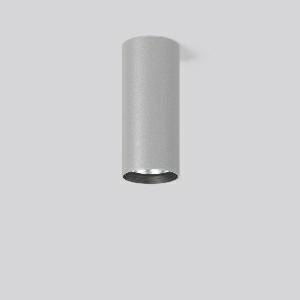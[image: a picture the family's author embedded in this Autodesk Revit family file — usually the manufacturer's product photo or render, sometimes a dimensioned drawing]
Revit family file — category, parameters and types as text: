
# Revit family: heledon_mini_a_931210_004_1_76_3fc2
name_source: partatom
category: Lighting Fixtures
units: mm (PartAtom-declared; Revit-internal decimal feet)

## family parameters
Cut with Voids When Loaded = No
Host = Face
Light Source = No
Part Type = Normal
Room Calculation Point = No
Round Connector Dimension = Use Diameter
Shared = No

## types (1)
- HELEDON mini A (1 x LED Modul 940, 3900 lm, 4000)
    Apparent Load = 29 VA
    Approval mark = CE
    CIE Flux Codes = 95 99 100 100 100
    Color Rendering = 92
    Color Temperature = 4000
    Default Elevation = 1800 mm
    Description = Series: HELEDON mini
Cylindrical surface-mounted downlight. Housing: die-cast aluminium, powder-coated. Internal ceiling frame polycarbonate with bayonet mounting. Black plastic ring and recessed LED to prevent glare from the side. Optical assembly with reflector made of MIRO-Silver with 98% total light reflection for outstanding efficiency - can be changed without tools. Best colour rendering index Ra>90. Suitable for Ceiling mounting. Easy installation with a separate ceiling frame with bayonet mounting and plug connection. Driver integrated. Connected via plug-in connector. High quality converter without flickering and stroboscopic effect. The following accessories can be mounted without use of tools: interchangeable lenses, decorative glasses, honeycomb louvre, clear and frosted diffusers, white interchangeable plastic ring. 
Colour: silver
Diameter: 87 mm
Height: 197 mm
Lamp: LED
Socket: without socket
Colour temperature: 4000K
Colour rendering index (CRI): 92
System power: 29 W
Rated luminous flux: 3900 lm
Luminous efficiency: 134 lm/W
Control gear: Converter, dimmable, DALI
Protection class: I
Type of protection: IP 20
    Height = 197 mm
    Lamp = 1 x LED Modul 940
    Lamp Light Flux = 3900 lm
    Lamp count = 1
    Length = 87 mm
    Lifetime = 50000 h
    Luminous efficacy = 134 lm/W
    Manufacturer = RZB
    ModVariant = No
    Model = 931210.004.1.76
    Mounting Place = Ceiling
    Mounting Type = Surface mounted
    Number of Poles = 1
    OnlyDefault = Yes
    Power Factor = 1
    Product Name = HELEDON mini A
    Product group = Surface mounted downlights
    ProductGroupID = 302
    Protection Class = Protection class I
    Protection Degree = IP 20
    RLX_Detail_Level = 1
    RLX_Emergency_Light_Flux = 0 lm
    RLX_Emergency_Type = 0
    RLX_Emergency_Type_DB = No
    RlxData = <blob elided: 107185 chars, md5=daccbc05>
    Socket = socket
    Standby Power = 0 W
    System Light Flux = 3900 lm
    System Power = 29 W
    Type Comments = Product without accessories
    Type Image = 931188.004.jpg
    URL = http://relux.com
    VarID = ---
    Voltage = 230 V
    Voltage Range = 220-240 V
    Weight = 0.00 kg
    Width = 0 mm  [stored 0 ft]

note: [stored X ft] marks values corroborated as IEEE doubles in the binary element streams (Revit-internal decimal feet)

## geometry (parser evidence)
native form markers: Blend x4, Sweep x8
no freeform markers — native parametric forms only
